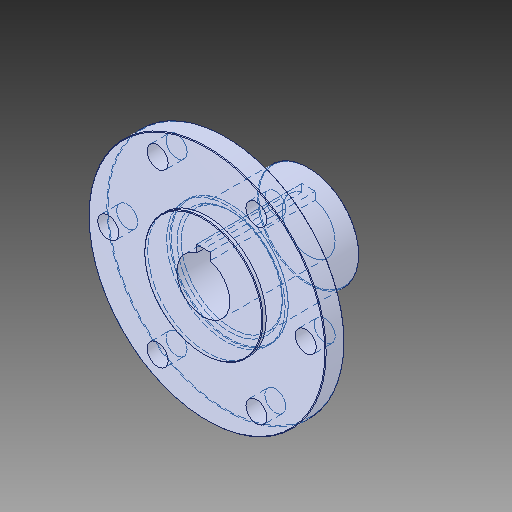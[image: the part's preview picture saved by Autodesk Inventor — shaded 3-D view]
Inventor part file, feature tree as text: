
AUTODESK INVENTOR PART (.ipt)
format: ipt  version: 2019 (Build 230136000, 136)  size: 169,472 bytes
history: native  units: in
note: dims shown in document units (in); Inventor stores cm internally (conversion verified against a paired STEP export)
features: chamfer x1
ambient origin geometry x8: Origin, YZ Plane, XZ Plane, XY Plane, X Axis, Y Axis, Z Axis, Center Point
bodies: Solid1 (feature_tree)
feature tree (1):
  chamfer  "Chamfer2"  [1 undecoded]
note: 1 required parameter value undecoded (feature->parameter linkage not recoverable at this tier; creation-order binding heuristic only, values carry confidence <= 0.55)
